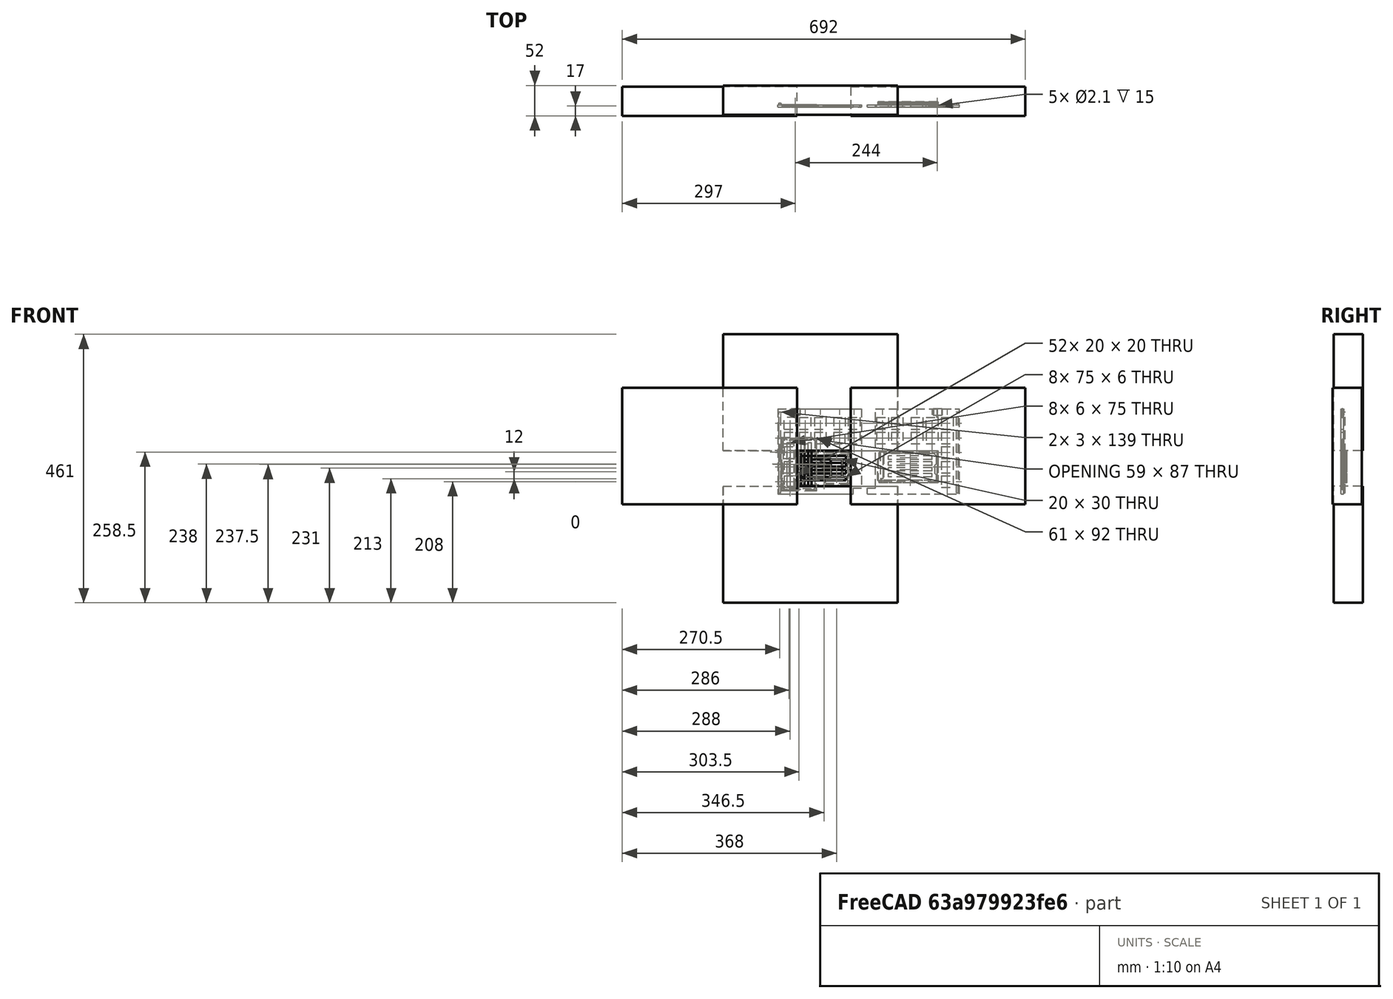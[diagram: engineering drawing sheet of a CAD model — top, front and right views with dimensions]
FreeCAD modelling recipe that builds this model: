
FCSTD DOCUMENT  (FreeCAD 0.17R13522 (Git))
Label: bases_para_arduino_matricia
License: CreativeCommons Attribution-ShareAlike
LicenseURL: http://creativecommons.org/licenses/by-sa/4.0/
objects: Part::Box×36, Part::Cut×22, Part::MultiFuse×14, Part::Feature×9
note: 81 computed .brp shape members not serialized (recipe doc carries the construction recipe); baked Part::Feature solids carry a one-line shape summary decoded from their .brp

FEATURE [Part::Feature] Cut001001001002003001008002002034017003001  label="base derecha001"
  Placement = pos=(-244,33,343) rot=(0,0,1;0rad)
  shape: bbox 176 x 9.04 x 212 mm, 484 faces (baked)
FEATURE [Part::Feature] Cut001001001002003001008002002034018001  label="base izquierda001"
  shape: bbox 144 x 9.04 x 212 mm, 478 faces (baked)
FEATURE [Part::Feature] Fusion011001  label="cortador matrizia001"
  Placement = pos=(232,-16.5,-238) rot=(1,0,0;1.5708rad)
  shape: bbox 87 x 3 x 59 mm, 54 faces (baked)
FEATURE [Part::Box] Box  label="Cube"
  AttacherType = Attacher::AttachEngine3D
  Height = 80
  Length = 226
  Placement = pos=(225,-21,-248) rot=(0,0,1;0rad)
  Width = 4
FEATURE [Part::Box] Box001  label="Cube001"
  AttacherType = Attacher::AttachEngine3D
  Height = 80
  Length = 226
  Placement = pos=(225,-21,-248) rot=(0,0,1;0rad)
  Width = 4
FEATURE [Part::MultiFuse] Fusion  label="derecha1"
  Placement = pos=(250,0,0) rot=(0,0,1;0rad)
  Refine = true
  Shapes = -> [Cut001001001002003001008002002034017003001,Box]
FEATURE [Part::MultiFuse] Fusion011002  label="izquierda1"
  Refine = true
  Shapes = -> [Box001,Cut001001001002003001008002002034018001]
FEATURE [Part::Cut] Cut
  Base = -> Fusion011002
  Refine = true
  Tool = -> Fusion011001
FEATURE [Part::Box] Box002  label="Cube002"
  AttacherType = Attacher::AttachEngine3D
  Height = 80
  Length = 226
  Placement = pos=(338,-21,-248) rot=(0,0,1;0rad)
  Width = 4
FEATURE [Part::Box] Box003  label="Cube003"
  AttacherType = Attacher::AttachEngine3D
  Height = 80
  Length = 226
  Placement = pos=(362,-21,-248) rot=(0,0,1;0rad)
  Width = 4
FEATURE [Part::Cut] Cut001001001002003001008002002034017003002  label="izquierda2"
  Base = -> Cut
  Refine = true
  Tool = -> Box002
FEATURE [Part::Cut] Cut001001001002003001008002002034017003003  label="derecha2"
  Base = -> Fusion
  Refine = true
  Tool = -> Box003
FEATURE [Part::Feature] Arduino_MEGA_Bumper_0003001_solid001001  label="mega_bumper001"
  Placement = pos=(694,-14.5,-234) rot=(0,0.707107,0.707107;3.14159rad)
  shape: bbox 103.5 x 5.08 x 55.22 mm, 538 faces (baked)
FEATURE [Part::MultiFuse] Fusion011003  label="derecha3"
  Placement = pos=(-250,0,0) rot=(0,0,1;0rad)
  Refine = true
  Shapes = -> [Cut001001001002003001008002002034017003003,Arduino_MEGA_Bumper_0003001_solid001001]
FEATURE [Part::Box] Box004  label="Cube004"
  AttacherType = Attacher::AttachEngine3D
  Height = 80
  Length = 800
  Placement = pos=(0,-24,-324) rot=(0,0,1;0rad)
  Width = 20
FEATURE [Part::Box] Box005  label="Cube005"
  AttacherType = Attacher::AttachEngine3D
  Height = 80
  Length = 800
  Placement = pos=(0,-24,-324) rot=(0,0,1;0rad)
  Width = 20
FEATURE [Part::Cut] Cut001001001002003001008002002034017003004  label="izq4"
  Base = -> Cut001001001002003001008002002034017003002
  Refine = true
  Tool = -> Box004
FEATURE [Part::Cut] Cut001001001002003001008002002034017003005  label="der4"
  Base = -> Fusion011003
  Refine = true
  Tool = -> Box005
FEATURE [Part::Box] Box006  label="Cube006"
  AttacherType = Attacher::AttachEngine3D
  Height = 10
  Length = 130
  Placement = pos=(194,-21,-254) rot=(0,0,1;0rad)
  Width = 4
FEATURE [Part::Box] Box007  label="Cube007"
  AttacherType = Attacher::AttachEngine3D
  Height = 10
  Length = 158
  Placement = pos=(324,-21,-254) rot=(0,0,1;0rad)
  Width = 4
FEATURE [Part::MultiFuse] Fusion011004  label="der5"
  Refine = true
  Shapes = -> [Box007,Cut001001001002003001008002002034017003005]
FEATURE [Part::MultiFuse] Fusion011005  label="izq5"
  Refine = true
  Shapes = -> [Cut001001001002003001008002002034017003004,Box006]
FEATURE [Part::Box] Box008  label="Cube008"
  AttacherType = Attacher::AttachEngine3D
  Height = 20
  Length = 20
  Placement = pos=(290,-28,-168) rot=(0,0,1;0rad)
  Width = 20
FEATURE [Part::Box] Box009  label="Cube009"
  AttacherType = Attacher::AttachEngine3D
  Height = 20
  Length = 20
  Placement = pos=(315,-28,-168) rot=(0,0,1;0rad)
  Width = 20
FEATURE [Part::Box] Box010  label="Cube010"
  AttacherType = Attacher::AttachEngine3D
  Height = 20
  Length = 20
  Placement = pos=(340,-28,-168) rot=(0,0,1;0rad)
  Width = 20
FEATURE [Part::Box] Box011  label="Cube011"
  AttacherType = Attacher::AttachEngine3D
  Height = 20
  Length = 20
  Placement = pos=(365,-28,-168) rot=(0,0,1;0rad)
  Width = 20
FEATURE [Part::Cut] Cut001001001002003001008002002034017003006
  Base = -> Fusion011005
  Refine = true
  Tool = -> Box009
FEATURE [Part::Cut] Cut001001001002003001008002002034017003007  label="izq6"
  Base = -> Cut001001001002003001008002002034017003006
  Refine = true
  Tool = -> Box008
FEATURE [Part::Cut] Cut001001001002003001008002002034017003008
  Base = -> Fusion011004
  Refine = true
  Tool = -> Box010
FEATURE [Part::Cut] Cut001001001002003001008002002034017003009  label="der6"
  Base = -> Cut001001001002003001008002002034017003008
  Refine = true
  Tool = -> Box011
FEATURE [Part::Box] Box012  label="Cube012"
  AttacherType = Attacher::AttachEngine3D
  Height = 1
  Length = 3
  Placement = pos=(362,-19,-168) rot=(0,0,1;0rad)
  Width = 2
FEATURE [Part::Box] Box013  label="Cube013"
  AttacherType = Attacher::AttachEngine3D
  Height = 1
  Length = 2
  Placement = pos=(338,-19,-168) rot=(0,0,1;0rad)
  Width = 2
FEATURE [Part::MultiFuse] Fusion011006
  Refine = true
  Shapes = -> [Cut001001001002003001008002002034017003009,Box012]
FEATURE [Part::Box] Box014  label="Cube014"
  AttacherType = Attacher::AttachEngine3D
  Height = 1
  Length = 2
  Placement = pos=(336,-19,-168) rot=(0,0,1;0rad)
  Width = 2
FEATURE [Part::MultiFuse] Fusion011007  label="der7"
  Refine = true
  Shapes = -> [Fusion011006,Box013]
FEATURE [Part::Box] Box015  label="Cube015"
  AttacherType = Attacher::AttachEngine3D
  Height = 1
  Length = 5
  Placement = pos=(310,-19,-168) rot=(0,0,1;0rad)
  Width = 2
FEATURE [Part::MultiFuse] Fusion011008
  Refine = true
  Shapes = -> [Cut001001001002003001008002002034017003007,Box014]
FEATURE [Part::MultiFuse] Fusion011009  label="izq7"
  Refine = true
  Shapes = -> [Fusion011008,Box015]
FEATURE [Part::Box] Box016  label="Cube016"
  AttacherType = Attacher::AttachEngine3D
  Height = 8
  Length = 3
  Placement = pos=(196,-17,-252) rot=(0,0,1;0rad)
  Width = 3
FEATURE [Part::Box] Box017  label="Cube017"
  AttacherType = Attacher::AttachEngine3D
  Height = 8
  Length = 3
  Placement = pos=(477,-17,-252) rot=(0,0,1;0rad)
  Width = 3
FEATURE [Part::MultiFuse] Fusion011010  label="der8"
  Refine = true
  Shapes = -> [Box017,Fusion011007]
FEATURE [Part::MultiFuse] Fusion011011  label="izq8"
  Refine = true
  Shapes = -> [Fusion011009,Box016]
FEATURE [Part::Box] Box018  label="Cube018"
  AttacherType = Attacher::AttachEngine3D
  Height = 6
  Length = 75
  Placement = pos=(236,-25,-195) rot=(0,0,1;0rad)
  Width = 20
FEATURE [Part::Box] Box019  label="Cube019"
  AttacherType = Attacher::AttachEngine3D
  Height = 6
  Length = 75
  Placement = pos=(236,-25,-207) rot=(0,0,1;0rad)
  Width = 20
FEATURE [Part::Box] Box020  label="Cube020"
  AttacherType = Attacher::AttachEngine3D
  Height = 6
  Length = 75
  Placement = pos=(236,-25,-219) rot=(0,0,1;0rad)
  Width = 20
FEATURE [Part::Box] Box021  label="Cube021"
  AttacherType = Attacher::AttachEngine3D
  Height = 6
  Length = 75
  Placement = pos=(236,-25,-231) rot=(0,0,1;0rad)
  Width = 20
FEATURE [Part::Box] Box022  label="Cube022"
  AttacherType = Attacher::AttachEngine3D
  Height = 6
  Length = 75
  Placement = pos=(360,-25,-195) rot=(0,0,1;0rad)
  Width = 20
FEATURE [Part::Box] Box023  label="Cube023"
  AttacherType = Attacher::AttachEngine3D
  Height = 6
  Length = 75
  Placement = pos=(360,-25,-205) rot=(0,0,1;0rad)
  Width = 20
FEATURE [Part::Box] Box024  label="Cube024"
  AttacherType = Attacher::AttachEngine3D
  Height = 6
  Length = 75
  Placement = pos=(360,-25,-215) rot=(0,0,1;0rad)
  Width = 20
FEATURE [Part::Box] Box025  label="Cube025"
  AttacherType = Attacher::AttachEngine3D
  Height = 6
  Length = 75
  Placement = pos=(360,-25,-225) rot=(0,0,1;0rad)
  Width = 20
FEATURE [Part::Cut] Cut001001001002003001008002002034017003010
  Base = -> Fusion011010
  Refine = true
  Tool = -> Box025
FEATURE [Part::Cut] Cut001001001002003001008002002034017003011
  Base = -> Cut001001001002003001008002002034017003010
  Refine = true
  Tool = -> Box024
FEATURE [Part::Cut] Cut001001001002003001008002002034017003012
  Base = -> Cut001001001002003001008002002034017003011
  Refine = true
  Tool = -> Box023
FEATURE [Part::Cut] Cut001001001002003001008002002034017003013  label="derecha"
  Base = -> Cut001001001002003001008002002034017003012
  Placement = pos=(24,0,0) rot=(0,0,1;0rad)
  Refine = true
  Tool = -> Box022
FEATURE [Part::Cut] Cut001001001002003001008002002034017003014
  Base = -> Fusion011011
  Refine = true
  Tool = -> Box021
FEATURE [Part::Cut] Cut001001001002003001008002002034017003015
  Base = -> Cut001001001002003001008002002034017003014
  Refine = true
  Tool = -> Box019
FEATURE [Part::Cut] Cut001001001002003001008002002034017003016
  Base = -> Cut001001001002003001008002002034017003015
  Refine = true
  Tool = -> Box020
FEATURE [Part::Cut] Cut001001001002003001008002002034017003017  label="izquierda"
  Base = -> Cut001001001002003001008002002034017003016
  Refine = true
  Tool = -> Box018
FEATURE [Part::Feature] Cut001001001002003001008002002034017003017001  label="izquierda_reformada"
  shape: bbox 144 x 7 x 146 mm, 143 faces (baked)
FEATURE [Part::Feature] Cut001001001002003001008002002034017003017001001  label="izquierda_reformada_base_matricia1"
  shape: bbox 144 x 7 x 146 mm, 143 faces (baked)
FEATURE [Part::Box] Box026  label="Cube026"
  AttacherType = Attacher::AttachEngine3D
  Height = 200
  Length = 300
  Placement = pos=(100,-34,-180) rot=(0,0,1;0rad)
  Width = 50
FEATURE [Part::Box] Box027  label="Cube027"
  AttacherType = Attacher::AttachEngine3D
  Height = 200
  Length = 300
  Placement = pos=(100,-34,-441) rot=(0,0,1;0rad)
  Width = 50
FEATURE [Part::Box] Box028  label="Cube028"
  AttacherType = Attacher::AttachEngine3D
  Height = 200
  Length = 300
  Placement = pos=(-73,-36,-272) rot=(0,0,1;0rad)
  Width = 50
FEATURE [Part::Box] Box029  label="Cube029"
  AttacherType = Attacher::AttachEngine3D
  Height = 200
  Length = 300
  Placement = pos=(319,-36,-272) rot=(0,0,1;0rad)
  Width = 50
FEATURE [Part::MultiFuse] Fusion011012
  Shapes = -> [Box029,Box026,Box028,Box027]
FEATURE [Part::Feature] Fusion011012001  label="Fusion011013"
  shape: bbox 692 x 52 x 461 mm, 24 faces (baked)
FEATURE [Part::Cut] Cut001001001002003001008002002034017003017001002  label="base_matricia_1"
  Base = -> Cut001001001002003001008002002034017003017001001
  Placement = pos=(441,0,70) rot=(0,1,0;1.5708rad)
  Tool = -> Fusion011012001
FEATURE [Part::Box] Box030  label="Cube030"
  AttacherType = Attacher::AttachEngine3D
  Height = 110
  Length = 112
  Placement = pos=(201,-21,-254) rot=(0,0,1;0rad)
  Width = 4
FEATURE [Part::Box] Box031  label="Cube031"
  AttacherType = Attacher::AttachEngine3D
  Height = 84
  Length = 20
  Placement = pos=(300,-21,-254) rot=(0,0,1;0rad)
  Width = 4
FEATURE [Part::MultiFuse] Fusion011012002
  Shapes = -> [Box031,Cut001001001002003001008002002034017003017001,Box030]
FEATURE [Part::Feature] Fusion011012002001  label="Fusion011012003"
  shape: bbox 144 x 7 x 146 mm, 46 faces (baked)
FEATURE [Part::Box] Box032  label="Cube032"
  AttacherType = Attacher::AttachEngine3D
  Height = 92
  Length = 61
  Placement = pos=(200,-21,-249) rot=(0,0,1;0rad)
  Width = 4
FEATURE [Part::Cut] Cut001001001002003001008002002034017003017001003
  Base = -> Fusion011012002001
  Tool = -> Box032
FEATURE [Part::MultiFuse] Fusion011012002002
  Shapes = -> [Cut001001001002003001008002002034017003017001002,Cut001001001002003001008002002034017003017001003]
FEATURE [Part::Feature] Fusion011012002002001  label="Fusion011012002003"
  shape: bbox 144 x 7 x 146 mm, 115 faces (baked)
FEATURE [Part::Box] Box033  label="Cube033"
  AttacherType = Attacher::AttachEngine3D
  Height = 20
  Length = 20
  Placement = pos=(290,-23,-168) rot=(0,0,1;0rad)
  Width = 10
FEATURE [Part::Box] Box034  label="Cube034"
  AttacherType = Attacher::AttachEngine3D
  Height = 50
  Length = 38
  Placement = pos=(276,-19,-236) rot=(0,0,1;0rad)
  Width = 2
FEATURE [Part::Cut] Cut001001001002003001008002002034017003017001004
  Base = -> Fusion011012002002001
  Tool = -> Box034
FEATURE [Part::Cut] Cut001001001002003001008002002034017003017001005  label="izquierda_nueva_con_dos_matricias"
  Base = -> Cut001001001002003001008002002034017003017001004
  Tool = -> Box033
FEATURE [Part::Box] Box035  label="Cube035"
  AttacherType = Attacher::AttachEngine3D
  Height = 30
  Length = 20
  Placement = pos=(285,-23,-225) rot=(0,0,1;0rad)
  Width = 10
FEATURE [Part::Cut] Cut001001001002003001008002002034017003017001006  label="izquierda_nueva_con_dos_matricias_final"
  Base = -> Cut001001001002003001008002002034017003017001005
  Tool = -> Box035
